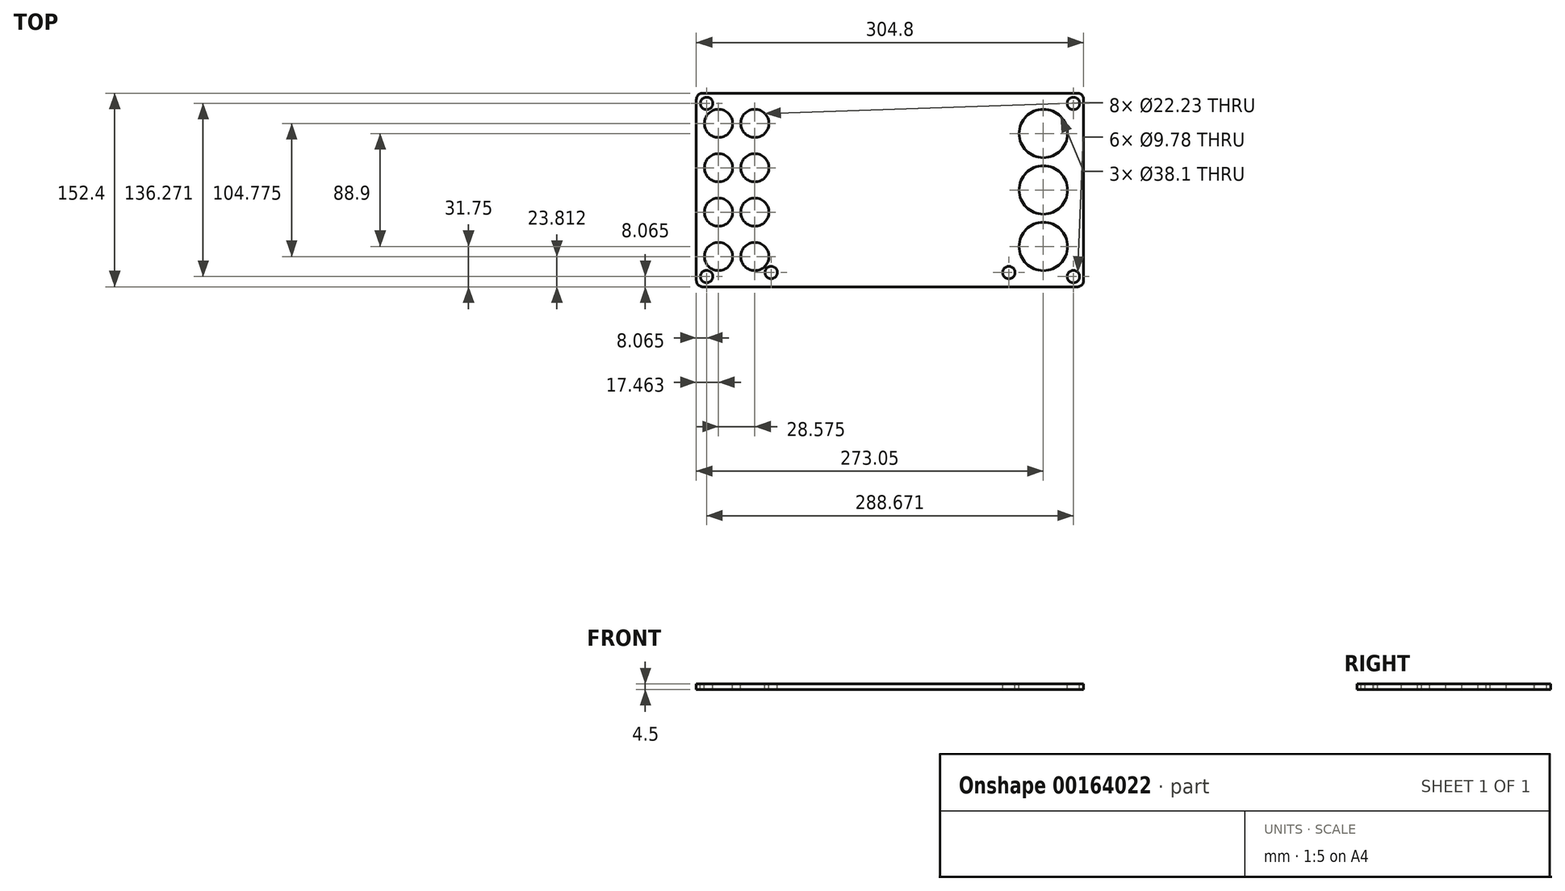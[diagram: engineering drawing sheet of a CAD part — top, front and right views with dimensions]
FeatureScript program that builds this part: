
annotation { "Feature Type Name" : "Feature", "Feature Type Description" : "" }
export const myFeature = defineFeature(function(context is Context, id is Id, definition is map)
    precondition{}
    {
        {
            var Q0;
            Q0=qCreatedBy(makeId("Top.planeOp"),FACE);
            var sketch = newSketch(context, id + "F0", { "sketchPlane" : qUnion([Q0])});
            skLineSegment(sketch, "E0.bottom", {"start": v(152.4, -76.2) * mm, "end": v(-152.4, -76.2) * mm});
            skLineSegment(sketch, "E0.top", {"start": v(152.4, 76.2) * mm, "end": v(-152.4, 76.2) * mm});
            skLineSegment(sketch, "E0.left", {"start": v(152.4, -76.2) * mm, "end": v(152.4, 76.2) * mm});
            skLineSegment(sketch, "E0.right", {"start": v(-152.4, -76.2) * mm, "end": v(-152.4, 76.2) * mm});
            skPoint(sketch, "E0.middle", {"position": v(0, 0) * mm});
            skSolve(sketch);
        }
        {
            var Q0;
            Q0=makeQuery(id+"F0.imprint","IMPRINT",FACE,{"disambiguationData":[TD([[makeQuery(id+"F0.imprint","IMPRINT",EDGE,{"derivedFrom":sQuery(id+"F0.wireOp",EDGE,"E0.bottom")}),-1.0]])]});
            extrude(context, id + "F1", {"entities" : qUnion([Q0]), "depth" : 4.5 * mm});
        }
        {
            var Q0;
            Q0=makeQuery(id+"F1.opExtrude","SWEPT_EDGE",EDGE,{"disambiguationData":[OSD([sQuery(id+"F0.wireOp",EDGE,"E0.top"),sQuery(id+"F0.wireOp",EDGE,"E0.right")])]});
            var Q1;
            Q1=makeQuery(id+"F1.opExtrude","SWEPT_EDGE",EDGE,{"disambiguationData":[OSD([sQuery(id+"F0.wireOp",EDGE,"E0.bottom"),sQuery(id+"F0.wireOp",EDGE,"E0.right")])]});
            var Q2;
            Q2=makeQuery(id+"F1.opExtrude","SWEPT_EDGE",EDGE,{"disambiguationData":[OSD([sQuery(id+"F0.wireOp",EDGE,"E0.bottom"),sQuery(id+"F0.wireOp",EDGE,"E0.left")])]});
            var Q3;
            Q3=makeQuery(id+"F1.opExtrude","SWEPT_EDGE",EDGE,{"disambiguationData":[OSD([sQuery(id+"F0.wireOp",EDGE,"E0.top"),sQuery(id+"F0.wireOp",EDGE,"E0.left")])]});
            fillet(context, id + "F2", {"entities" : qUnion([Q0, Q1, Q2, Q3]), "radius" : 5.08 * mm, "tangentPropagation" : true, "allowEdgeOverflow" : false});
        }
        {
            var Q0;
            Q0=makeQuery(id+"F1.opExtrude","CAP_FACE",FACE,{"disambiguationData":[OSD([sQuery(id+"F0.wireOp",EDGE,"E0.bottom"),sQuery(id+"F0.wireOp",EDGE,"E0.top"),sQuery(id+"F0.wireOp",EDGE,"E0.left"),sQuery(id+"F0.wireOp",EDGE,"E0.right")])],"isStart":false});
            var sketch = newSketch(context, id + "F3", { "sketchPlane" : qUnion([Q0])});
            skCircle(sketch, "E1", {"center": v(-144.34, 68.14) * mm, "radius": 4.89 * mm});
            skCircle(sketch, "E2", {"center": v(-144.34, -68.14) * mm, "radius": 4.89 * mm});
            skCircle(sketch, "E3", {"center": v(144.34, -68.14) * mm, "radius": 4.89 * mm});
            skCircle(sketch, "E4", {"center": v(144.34, 68.14) * mm, "radius": 4.89 * mm});
            skSolve(sketch);
        }
        {
            var Q0;
            Q0 = qSketchRegion(id + "F3", true);
            extrude(context, id + "F4", {"entities" : qUnion([Q0]), "operationType" : NewBodyOperationType.REMOVE, "endBound" : BoundingType.THROUGH_ALL, "oppositeDirection" : true, "depth" : 25.4 * mm});
        }
        {
            var Q0;
            Q0=makeQuery(id+"F1.opExtrude","CAP_FACE",FACE,{"disambiguationData":[OSD([sQuery(id+"F0.wireOp",EDGE,"E0.bottom"),sQuery(id+"F0.wireOp",EDGE,"E0.top"),sQuery(id+"F0.wireOp",EDGE,"E0.left"),sQuery(id+"F0.wireOp",EDGE,"E0.right")])],"isStart":false});
            var sketch = newSketch(context, id + "F5", { "sketchPlane" : qUnion([Q0])});
            skCircle(sketch, "E5", {"center": v(-106.36, 52.39) * mm, "radius": 11.11 * mm});
            skCircle(sketch, "E6", {"center": v(-134.94, 52.39) * mm, "radius": 11.11 * mm});
            skCircle(sketch, "E7", {"center": v(-134.94, 17.46) * mm, "radius": 11.11 * mm});
            skCircle(sketch, "E8", {"center": v(-106.36, 17.47) * mm, "radius": 11.11 * mm});
            skCircle(sketch, "E9", {"center": v(-134.94, -17.46) * mm, "radius": 11.11 * mm});
            skCircle(sketch, "E10", {"center": v(-106.36, -17.46) * mm, "radius": 11.11 * mm});
            skCircle(sketch, "E11", {"center": v(-134.94, -52.39) * mm, "radius": 11.11 * mm});
            skCircle(sketch, "E12", {"center": v(-106.36, -52.39) * mm, "radius": 11.11 * mm});
            skSolve(sketch);
        }
        {
            var Q0;
            Q0 = qSketchRegion(id + "F5", true);
            extrude(context, id + "F6", {"entities" : qUnion([Q0]), "operationType" : NewBodyOperationType.REMOVE, "endBound" : BoundingType.THROUGH_ALL, "oppositeDirection" : true, "depth" : 25.4 * mm});
        }
        {
            var Q0;
            Q0=makeQuery(id+"F1.opExtrude","CAP_FACE",FACE,{"disambiguationData":[OSD([sQuery(id+"F0.wireOp",EDGE,"E0.bottom"),sQuery(id+"F0.wireOp",EDGE,"E0.top"),sQuery(id+"F0.wireOp",EDGE,"E0.left"),sQuery(id+"F0.wireOp",EDGE,"E0.right")])],"isStart":false});
            var sketch = newSketch(context, id + "F7", { "sketchPlane" : qUnion([Q0])});
            skCircle(sketch, "E13", {"center": v(120.65, 44.45) * mm, "radius": 19.05 * mm});
            skCircle(sketch, "E14", {"center": v(120.65, 0) * mm, "radius": 19.05 * mm});
            skCircle(sketch, "E15", {"center": v(120.65, -44.45) * mm, "radius": 19.05 * mm});
            skSolve(sketch);
        }
        {
            var Q0;
            Q0 = qSketchRegion(id + "F7", true);
            extrude(context, id + "F8", {"entities" : qUnion([Q0]), "operationType" : NewBodyOperationType.REMOVE, "endBound" : BoundingType.THROUGH_ALL, "oppositeDirection" : true, "depth" : 25.4 * mm});
        }
        {
            var Q0;
            Q0=makeQuery(id+"F1.opExtrude","CAP_FACE",FACE,{"disambiguationData":[OSD([sQuery(id+"F0.wireOp",EDGE,"E0.bottom"),sQuery(id+"F0.wireOp",EDGE,"E0.top"),sQuery(id+"F0.wireOp",EDGE,"E0.left"),sQuery(id+"F0.wireOp",EDGE,"E0.right")])],"isStart":false});
            var sketch = newSketch(context, id + "F9", { "sketchPlane" : qUnion([Q0])});
            skCircle(sketch, "E16", {"center": v(-93.54, -64.96) * mm, "radius": 4.89 * mm});
            skCircle(sketch, "E17", {"center": v(93.54, -64.96) * mm, "radius": 4.89 * mm});
            skSolve(sketch);
        }
        {
            var Q0;
            Q0 = qSketchRegion(id + "F9", true);
            extrude(context, id + "F10", {"entities" : qUnion([Q0]), "operationType" : NewBodyOperationType.REMOVE, "endBound" : BoundingType.THROUGH_ALL, "oppositeDirection" : true, "depth" : 25.4 * mm});
        }
    });
